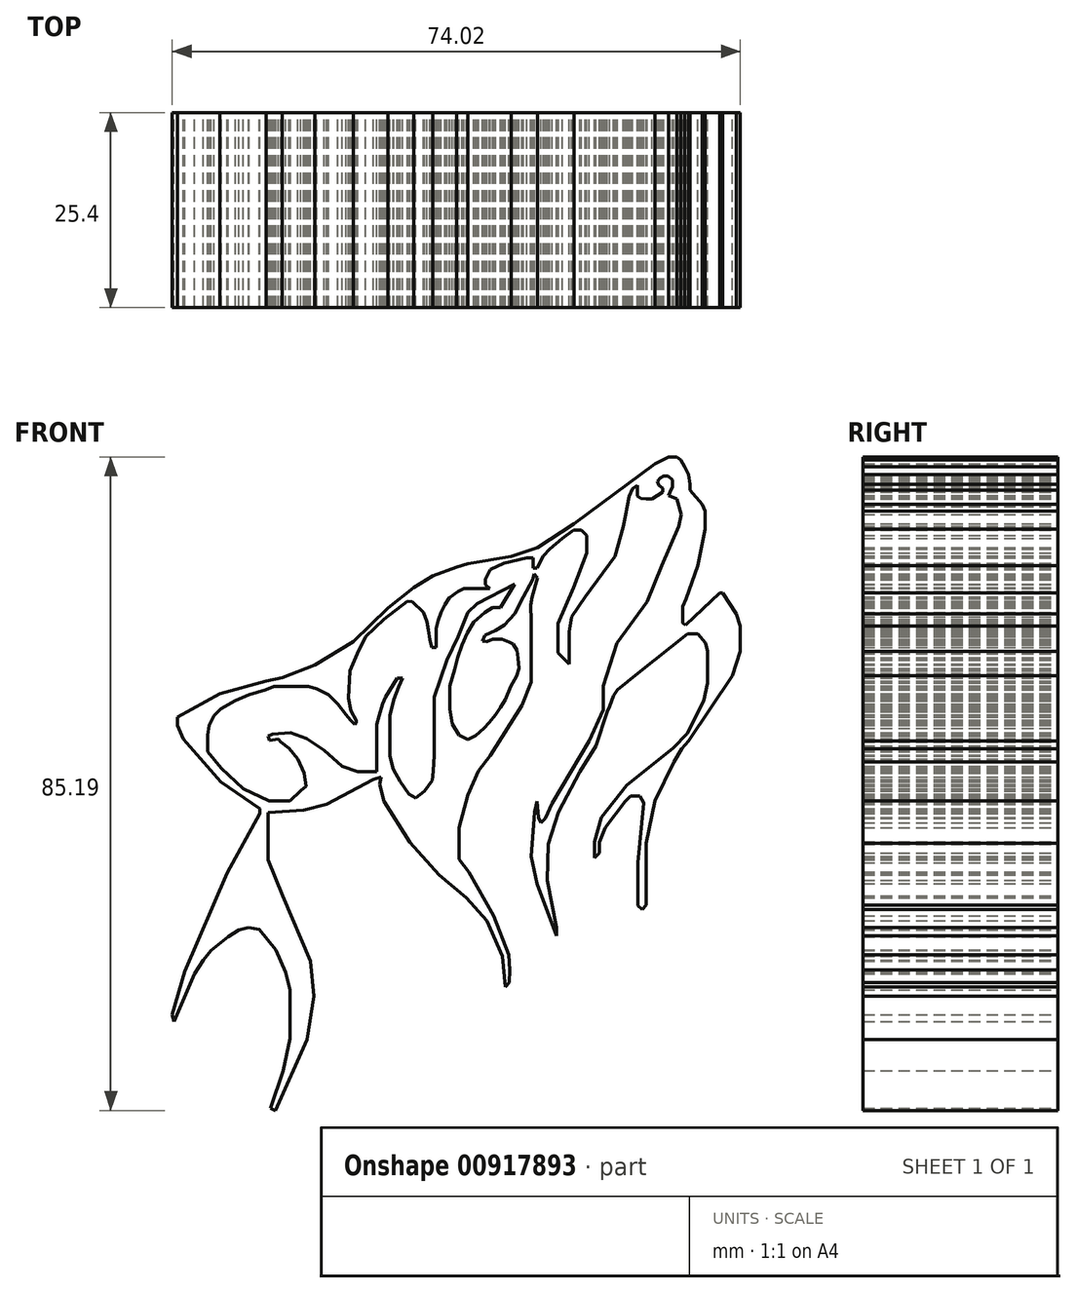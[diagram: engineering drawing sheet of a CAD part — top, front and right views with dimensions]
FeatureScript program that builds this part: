
annotation { "Feature Type Name" : "Feature", "Feature Type Description" : "" }
export const myFeature = defineFeature(function(context is Context, id is Id, definition is map)
    precondition{}
    {
        {
            var Q0;
            Q0=qCreatedBy(makeId("Front.planeOp"),FACE);
            var sketch = newSketch(context, id + "F0", { "sketchPlane" : qUnion([Q0])});
            skLineSegment(sketch, "E0", {"start": v(-38.5, -15.53) * mm, "end": v(-36.88, -9.84) * mm});
            skLineSegment(sketch, "E1", {"start": v(-36.88, -9.84) * mm, "end": v(-31.3, 2.95) * mm});
            skLineSegment(sketch, "E2", {"start": v(-31.3, 2.95) * mm, "end": v(-27.1, 10.73) * mm});
            skLineSegment(sketch, "E3", {"start": v(-27.1, 10.73) * mm, "end": v(-27.1, 11.36) * mm});
            skLineSegment(sketch, "E4", {"start": v(-27.1, 11.36) * mm, "end": v(-32.14, 14.82) * mm});
            skLineSegment(sketch, "E5", {"start": v(-32.14, 14.82) * mm, "end": v(-37.06, 20.41) * mm});
            skLineSegment(sketch, "E6", {"start": v(-37.06, 20.41) * mm, "end": v(-37.8, 22.21) * mm});
            skLineSegment(sketch, "E7", {"start": v(-37.8, 22.21) * mm, "end": v(-37.8, 23.3) * mm});
            skLineSegment(sketch, "E8", {"start": v(-37.8, 23.3) * mm, "end": v(-32.31, 26.36) * mm});
            skLineSegment(sketch, "E9", {"start": v(-32.31, 26.36) * mm, "end": v(-26.28, 28) * mm});
            skLineSegment(sketch, "E10", {"start": v(-26.28, 28) * mm, "end": v(-24.14, 28.41) * mm});
            skLineSegment(sketch, "E11", {"start": v(-24.14, 28.41) * mm, "end": v(-19.93, 30.06) * mm});
            skLineSegment(sketch, "E12", {"start": v(-19.93, 30.06) * mm, "end": v(-14.86, 33.12) * mm});
            skLineSegment(sketch, "E13", {"start": v(-14.86, 33.12) * mm, "end": v(-10.37, 37.53) * mm});
            skLineSegment(sketch, "E14", {"start": v(-10.37, 37.53) * mm, "end": v(-7.02, 40.16) * mm});
            skLineSegment(sketch, "E15", {"start": v(-7.02, 40.16) * mm, "end": v(-4.55, 41.68) * mm});
            skLineSegment(sketch, "E16", {"start": v(-4.55, 41.68) * mm, "end": v(-1.43, 42.86) * mm});
            skLineSegment(sketch, "E17", {"start": v(-1.43, 42.86) * mm, "end": v(0, 43.31) * mm});
            skLineSegment(sketch, "E18", {"start": v(0, 43.31) * mm, "end": v(5.68, 44.23) * mm});
            skLineSegment(sketch, "E19", {"start": v(5.68, 44.23) * mm, "end": v(9.13, 45.4) * mm});
            skLineSegment(sketch, "E20", {"start": v(9.13, 45.4) * mm, "end": v(13.88, 48.46) * mm});
            skLineSegment(sketch, "E21", {"start": v(13.88, 48.46) * mm, "end": v(24.44, 56.3) * mm});
            skLineSegment(sketch, "E22", {"start": v(24.44, 56.3) * mm, "end": v(26.17, 57.2) * mm});
            skLineSegment(sketch, "E23", {"start": v(26.17, 57.2) * mm, "end": v(27.25, 57.2) * mm});
            skLineSegment(sketch, "E24", {"start": v(27.25, 57.2) * mm, "end": v(27.75, 56.8) * mm});
            skLineSegment(sketch, "E25", {"start": v(27.75, 56.8) * mm, "end": v(28.27, 55.93) * mm});
            skLineSegment(sketch, "E26", {"start": v(28.27, 55.93) * mm, "end": v(28.77, 54.9) * mm});
            skLineSegment(sketch, "E27", {"start": v(28.77, 54.9) * mm, "end": v(28.96, 53.66) * mm});
            skLineSegment(sketch, "E28", {"start": v(28.96, 53.66) * mm, "end": v(28.96, 52.88) * mm});
            skLineSegment(sketch, "E29", {"start": v(28.96, 52.88) * mm, "end": v(30.55, 51) * mm});
            skLineSegment(sketch, "E30", {"start": v(30.55, 51) * mm, "end": v(30.97, 50.12) * mm});
            skLineSegment(sketch, "E31", {"start": v(30.97, 50.12) * mm, "end": v(30.97, 47.77) * mm});
            skLineSegment(sketch, "E32", {"start": v(30.97, 47.77) * mm, "end": v(30, 43.06) * mm});
            skLineSegment(sketch, "E33", {"start": v(30, 43.06) * mm, "end": v(28.46, 38.73) * mm});
            skLineSegment(sketch, "E34", {"start": v(28.46, 38.73) * mm, "end": v(28.05, 37.7) * mm});
            skLineSegment(sketch, "E35", {"start": v(28.05, 37.7) * mm, "end": v(28.05, 36.88) * mm});
            skLineSegment(sketch, "E36", {"start": v(28.05, 36.88) * mm, "end": v(28.05, 35.54) * mm});
            skLineSegment(sketch, "E37", {"start": v(28.05, 35.54) * mm, "end": v(28.4, 35.26) * mm});
            skLineSegment(sketch, "E38", {"start": v(28.4, 35.26) * mm, "end": v(32.85, 39.46) * mm});
            skLineSegment(sketch, "E39", {"start": v(32.85, 39.46) * mm, "end": v(33.27, 39.46) * mm});
            skLineSegment(sketch, "E40", {"start": v(33.27, 39.46) * mm, "end": v(35.03, 36.78) * mm});
            skLineSegment(sketch, "E41", {"start": v(35.03, 36.78) * mm, "end": v(35.53, 35.19) * mm});
            skLineSegment(sketch, "E42", {"start": v(35.53, 35.19) * mm, "end": v(35.53, 31.87) * mm});
            skLineSegment(sketch, "E43", {"start": v(35.53, 31.87) * mm, "end": v(34.48, 28.7) * mm});
            skLineSegment(sketch, "E44", {"start": v(34.48, 28.7) * mm, "end": v(32.17, 25.26) * mm});
            skLineSegment(sketch, "E45", {"start": v(32.17, 25.26) * mm, "end": v(28.77, 20.2) * mm});
            skLineSegment(sketch, "E46", {"start": v(28.77, 20.2) * mm, "end": v(27.93, 19.14) * mm});
            skLineSegment(sketch, "E47", {"start": v(27.93, 19.14) * mm, "end": v(26.86, 17.45) * mm});
            skLineSegment(sketch, "E48", {"start": v(26.86, 17.45) * mm, "end": v(24.38, 12.35) * mm});
            skLineSegment(sketch, "E49", {"start": v(24.38, 12.35) * mm, "end": v(23.84, 9.71) * mm});
            skLineSegment(sketch, "E50", {"start": v(23.84, 9.71) * mm, "end": v(23.24, 6.84) * mm});
            skLineSegment(sketch, "E51", {"start": v(23.24, 6.84) * mm, "end": v(23.24, 5.26) * mm});
            skLineSegment(sketch, "E52", {"start": v(23.24, 5.26) * mm, "end": v(23.24, -1.23) * mm});
            skLineSegment(sketch, "E53", {"start": v(23.24, -1.23) * mm, "end": v(22.78, -1.77) * mm});
            skLineSegment(sketch, "E54", {"start": v(22.78, -1.77) * mm, "end": v(22.22, -1.3) * mm});
            skLineSegment(sketch, "E55", {"start": v(22.22, -1.3) * mm, "end": v(22.22, 4.3) * mm});
            skLineSegment(sketch, "E56", {"start": v(22.22, 4.3) * mm, "end": v(22.95, 12.08) * mm});
            skLineSegment(sketch, "E57", {"start": v(22.95, 12.08) * mm, "end": v(22.46, 13) * mm});
            skLineSegment(sketch, "E58", {"start": v(22.46, 13) * mm, "end": v(21.22, 13) * mm});
            skLineSegment(sketch, "E59", {"start": v(21.22, 13) * mm, "end": v(20.51, 12.3) * mm});
            skLineSegment(sketch, "E60", {"start": v(20.51, 12.3) * mm, "end": v(17.91, 8.84) * mm});
            skLineSegment(sketch, "E61", {"start": v(17.91, 8.84) * mm, "end": v(17.16, 6.94) * mm});
            skLineSegment(sketch, "E62", {"start": v(17.16, 6.94) * mm, "end": v(17.16, 5.54) * mm});
            skLineSegment(sketch, "E63", {"start": v(17.16, 5.54) * mm, "end": v(16.56, 4.94) * mm});
            skLineSegment(sketch, "E64", {"start": v(16.56, 4.94) * mm, "end": v(16.56, 7) * mm});
            skLineSegment(sketch, "E65", {"start": v(16.56, 7) * mm, "end": v(17.43, 10.2) * mm});
            skLineSegment(sketch, "E66", {"start": v(17.43, 10.2) * mm, "end": v(20.73, 14.41) * mm});
            skLineSegment(sketch, "E67", {"start": v(20.73, 14.41) * mm, "end": v(26.84, 19.28) * mm});
            skLineSegment(sketch, "E68", {"start": v(26.84, 19.28) * mm, "end": v(28.6, 21.13) * mm});
            skLineSegment(sketch, "E69", {"start": v(28.6, 21.13) * mm, "end": v(30.76, 25.4) * mm});
            skLineSegment(sketch, "E70", {"start": v(30.76, 25.4) * mm, "end": v(31.3, 27.72) * mm});
            skLineSegment(sketch, "E71", {"start": v(31.3, 27.72) * mm, "end": v(31.3, 29.81) * mm});
            skLineSegment(sketch, "E72", {"start": v(31.3, 29.81) * mm, "end": v(31.3, 31.88) * mm});
            skLineSegment(sketch, "E73", {"start": v(31.3, 31.88) * mm, "end": v(31.02, 32.96) * mm});
            skLineSegment(sketch, "E74", {"start": v(31.02, 32.96) * mm, "end": v(29.98, 34.12) * mm});
            skLineSegment(sketch, "E75", {"start": v(29.98, 34.12) * mm, "end": v(28.64, 34.12) * mm});
            skLineSegment(sketch, "E76", {"start": v(28.64, 34.12) * mm, "end": v(22.17, 29.01) * mm});
            skLineSegment(sketch, "E77", {"start": v(22.17, 29.01) * mm, "end": v(19.53, 26.84) * mm});
            skLineSegment(sketch, "E78", {"start": v(19.53, 26.84) * mm, "end": v(19.02, 26.1) * mm});
            skLineSegment(sketch, "E79", {"start": v(19.02, 26.1) * mm, "end": v(18.48, 24.67) * mm});
            skLineSegment(sketch, "E80", {"start": v(18.48, 24.67) * mm, "end": v(18.18, 24) * mm});
            skLineSegment(sketch, "E81", {"start": v(18.18, 24) * mm, "end": v(17.67, 24.23) * mm});
            skLineSegment(sketch, "E82", {"start": v(17.67, 24.23) * mm, "end": v(17.67, 27.37) * mm});
            skLineSegment(sketch, "E83", {"start": v(17.67, 27.37) * mm, "end": v(19.45, 32.92) * mm});
            skLineSegment(sketch, "E84", {"start": v(19.45, 32.92) * mm, "end": v(23.42, 38.36) * mm});
            skLineSegment(sketch, "E85", {"start": v(23.42, 38.36) * mm, "end": v(25.3, 43.03) * mm});
            skLineSegment(sketch, "E86", {"start": v(25.3, 43.03) * mm, "end": v(27.5, 48.16) * mm});
            skLineSegment(sketch, "E87", {"start": v(27.5, 48.16) * mm, "end": v(27.86, 49.72) * mm});
            skLineSegment(sketch, "E88", {"start": v(27.86, 49.72) * mm, "end": v(27.25, 51.74) * mm});
            skLineSegment(sketch, "E89", {"start": v(27.25, 51.74) * mm, "end": v(26.17, 52.2) * mm});
            skLineSegment(sketch, "E90", {"start": v(26.17, 52.2) * mm, "end": v(26.35, 52.6) * mm});
            skLineSegment(sketch, "E91", {"start": v(26.35, 52.6) * mm, "end": v(26.7, 53.3) * mm});
            skLineSegment(sketch, "E92", {"start": v(26.7, 53.3) * mm, "end": v(26.7, 54.22) * mm});
            skLineSegment(sketch, "E93", {"start": v(26.7, 54.22) * mm, "end": v(26.15, 54.7) * mm});
            skLineSegment(sketch, "E94", {"start": v(26.15, 54.7) * mm, "end": v(25.56, 54.7) * mm});
            skLineSegment(sketch, "E95", {"start": v(25.56, 54.7) * mm, "end": v(25.08, 54.48) * mm});
            skLineSegment(sketch, "E96", {"start": v(25.08, 54.48) * mm, "end": v(24.72, 54.04) * mm});
            skLineSegment(sketch, "E97", {"start": v(24.72, 54.04) * mm, "end": v(24.94, 53.52) * mm});
            skLineSegment(sketch, "E98", {"start": v(24.94, 53.52) * mm, "end": v(25.42, 53.15) * mm});
            skLineSegment(sketch, "E99", {"start": v(25.42, 53.15) * mm, "end": v(25.42, 52.6) * mm});
            skLineSegment(sketch, "E100", {"start": v(25.42, 52.6) * mm, "end": v(24.01, 51.72) * mm});
            skLineSegment(sketch, "E101", {"start": v(24.01, 51.72) * mm, "end": v(23.28, 51.72) * mm});
            skLineSegment(sketch, "E102", {"start": v(23.28, 51.72) * mm, "end": v(22.54, 51.79) * mm});
            skLineSegment(sketch, "E103", {"start": v(22.54, 51.79) * mm, "end": v(22.13, 52.12) * mm});
            skLineSegment(sketch, "E104", {"start": v(22.13, 52.12) * mm, "end": v(22.1, 52.86) * mm});
            skLineSegment(sketch, "E105", {"start": v(22.1, 52.86) * mm, "end": v(22.1, 53.52) * mm});
            skLineSegment(sketch, "E106", {"start": v(22.1, 53.52) * mm, "end": v(21.47, 53.04) * mm});
            skLineSegment(sketch, "E107", {"start": v(21.47, 53.04) * mm, "end": v(21.03, 52.05) * mm});
            skLineSegment(sketch, "E108", {"start": v(21.03, 52.05) * mm, "end": v(20.8, 50.72) * mm});
            skLineSegment(sketch, "E109", {"start": v(20.8, 50.72) * mm, "end": v(20.62, 49.72) * mm});
            skLineSegment(sketch, "E110", {"start": v(20.62, 49.72) * mm, "end": v(20.29, 48.1) * mm});
            skLineSegment(sketch, "E111", {"start": v(20.29, 48.1) * mm, "end": v(19.22, 44.27) * mm});
            skLineSegment(sketch, "E112", {"start": v(19.22, 44.27) * mm, "end": v(15.35, 38.95) * mm});
            skLineSegment(sketch, "E113", {"start": v(15.35, 38.95) * mm, "end": v(13.54, 36.37) * mm});
            skLineSegment(sketch, "E114", {"start": v(13.54, 36.37) * mm, "end": v(13.2, 34.38) * mm});
            skLineSegment(sketch, "E115", {"start": v(13.2, 34.38) * mm, "end": v(13.2, 31.28) * mm});
            skLineSegment(sketch, "E116", {"start": v(13.2, 31.28) * mm, "end": v(13.2, 30.2) * mm});
            skLineSegment(sketch, "E117", {"start": v(13.2, 30.2) * mm, "end": v(11.8, 31.65) * mm});
            skLineSegment(sketch, "E118", {"start": v(11.8, 31.65) * mm, "end": v(11.8, 35.45) * mm});
            skLineSegment(sketch, "E119", {"start": v(11.8, 35.45) * mm, "end": v(13.79, 40.15) * mm});
            skLineSegment(sketch, "E120", {"start": v(13.79, 40.15) * mm, "end": v(15.55, 44.66) * mm});
            skLineSegment(sketch, "E121", {"start": v(15.55, 44.66) * mm, "end": v(15.55, 46.96) * mm});
            skLineSegment(sketch, "E122", {"start": v(15.55, 46.96) * mm, "end": v(14.81, 47.7) * mm});
            skLineSegment(sketch, "E123", {"start": v(14.81, 47.7) * mm, "end": v(13.78, 47.7) * mm});
            skLineSegment(sketch, "E124", {"start": v(13.78, 47.7) * mm, "end": v(12.37, 46.56) * mm});
            skLineSegment(sketch, "E125", {"start": v(12.37, 46.56) * mm, "end": v(10.73, 45.2) * mm});
            skLineSegment(sketch, "E126", {"start": v(10.73, 45.2) * mm, "end": v(9.88, 44.3) * mm});
            skLineSegment(sketch, "E127", {"start": v(9.88, 44.3) * mm, "end": v(9.03, 42.71) * mm});
            skLineSegment(sketch, "E128", {"start": v(9.03, 42.71) * mm, "end": v(8.56, 42.71) * mm});
            skLineSegment(sketch, "E129", {"start": v(8.56, 42.71) * mm, "end": v(8.56, 44.03) * mm});
            skLineSegment(sketch, "E130", {"start": v(8.56, 44.03) * mm, "end": v(7.72, 44.03) * mm});
            skLineSegment(sketch, "E131", {"start": v(7.72, 44.03) * mm, "end": v(4.71, 43.37) * mm});
            skLineSegment(sketch, "E132", {"start": v(4.71, 43.37) * mm, "end": v(2.98, 42.53) * mm});
            skLineSegment(sketch, "E133", {"start": v(2.98, 42.53) * mm, "end": v(2.32, 41.26) * mm});
            skLineSegment(sketch, "E134", {"start": v(2.32, 41.26) * mm, "end": v(2.32, 40.55) * mm});
            skLineSegment(sketch, "E135", {"start": v(2.32, 40.55) * mm, "end": v(2.88, 40.04) * mm});
            skLineSegment(sketch, "E136", {"start": v(2.88, 40.04) * mm, "end": v(-0.45, 40.04) * mm});
            skLineSegment(sketch, "E137", {"start": v(-0.45, 40.04) * mm, "end": v(-1.26, 39.64) * mm});
            skLineSegment(sketch, "E138", {"start": v(-1.26, 39.64) * mm, "end": v(-2.36, 38.86) * mm});
            skLineSegment(sketch, "E139", {"start": v(-2.36, 38.86) * mm, "end": v(-2.95, 37.97) * mm});
            skLineSegment(sketch, "E140", {"start": v(-2.95, 37.97) * mm, "end": v(-3.5, 36.97) * mm});
            skLineSegment(sketch, "E141", {"start": v(-3.5, 36.97) * mm, "end": v(-3.86, 35.84) * mm});
            skLineSegment(sketch, "E142", {"start": v(-3.86, 35.84) * mm, "end": v(-4.08, 34.86) * mm});
            skLineSegment(sketch, "E143", {"start": v(-4.08, 34.86) * mm, "end": v(-4.08, 33.83) * mm});
            skLineSegment(sketch, "E144", {"start": v(-4.08, 33.83) * mm, "end": v(-4.08, 32.35) * mm});
            skLineSegment(sketch, "E145", {"start": v(-4.08, 32.35) * mm, "end": v(-4.65, 32.35) * mm});
            skLineSegment(sketch, "E146", {"start": v(-4.65, 32.35) * mm, "end": v(-4.92, 33.36) * mm});
            skLineSegment(sketch, "E147", {"start": v(-4.92, 33.36) * mm, "end": v(-5.14, 34.64) * mm});
            skLineSegment(sketch, "E148", {"start": v(-5.14, 34.64) * mm, "end": v(-5.33, 35.72) * mm});
            skLineSegment(sketch, "E149", {"start": v(-5.33, 35.72) * mm, "end": v(-5.73, 36.97) * mm});
            skLineSegment(sketch, "E150", {"start": v(-5.73, 36.97) * mm, "end": v(-7.2, 38.34) * mm});
            skLineSegment(sketch, "E151", {"start": v(-7.2, 38.34) * mm, "end": v(-7.86, 38.37) * mm});
            skLineSegment(sketch, "E152", {"start": v(-7.86, 38.37) * mm, "end": v(-10.93, 36.06) * mm});
            skLineSegment(sketch, "E153", {"start": v(-10.93, 36.06) * mm, "end": v(-13.28, 33.75) * mm});
            skLineSegment(sketch, "E154", {"start": v(-13.28, 33.75) * mm, "end": v(-14.4, 31.5) * mm});
            skLineSegment(sketch, "E155", {"start": v(-14.4, 31.5) * mm, "end": v(-15.3, 29.3) * mm});
            skLineSegment(sketch, "E156", {"start": v(-15.3, 29.3) * mm, "end": v(-15.54, 25.76) * mm});
            skLineSegment(sketch, "E157", {"start": v(-15.54, 25.76) * mm, "end": v(-15.24, 24.1) * mm});
            skLineSegment(sketch, "E158", {"start": v(-15.24, 24.1) * mm, "end": v(-14.54, 22.83) * mm});
            skLineSegment(sketch, "E159", {"start": v(-14.54, 22.83) * mm, "end": v(-14.54, 22.53) * mm});
            skLineSegment(sketch, "E160", {"start": v(-14.54, 22.53) * mm, "end": v(-14.72, 22.34) * mm});
            skLineSegment(sketch, "E161", {"start": v(-14.72, 22.34) * mm, "end": v(-15.27, 22.9) * mm});
            skLineSegment(sketch, "E162", {"start": v(-15.27, 22.9) * mm, "end": v(-15.87, 23.63) * mm});
            skLineSegment(sketch, "E163", {"start": v(-15.87, 23.63) * mm, "end": v(-16.93, 24.97) * mm});
            skLineSegment(sketch, "E164", {"start": v(-16.93, 24.97) * mm, "end": v(-18.1, 26.2) * mm});
            skLineSegment(sketch, "E165", {"start": v(-18.1, 26.2) * mm, "end": v(-19.67, 26.98) * mm});
            skLineSegment(sketch, "E166", {"start": v(-19.67, 26.98) * mm, "end": v(-20.73, 27.29) * mm});
            skLineSegment(sketch, "E167", {"start": v(-20.73, 27.29) * mm, "end": v(-25.27, 27.29) * mm});
            skLineSegment(sketch, "E168", {"start": v(-25.27, 27.29) * mm, "end": v(-26.35, 26.84) * mm});
            skLineSegment(sketch, "E169", {"start": v(-26.35, 26.84) * mm, "end": v(-28.49, 26.19) * mm});
            skLineSegment(sketch, "E170", {"start": v(-28.49, 26.19) * mm, "end": v(-30.24, 25.44) * mm});
            skLineSegment(sketch, "E171", {"start": v(-30.24, 25.44) * mm, "end": v(-32.14, 24.4) * mm});
            skLineSegment(sketch, "E172", {"start": v(-32.14, 24.4) * mm, "end": v(-33.05, 23.5) * mm});
            skLineSegment(sketch, "E173", {"start": v(-33.05, 23.5) * mm, "end": v(-33.66, 22.2) * mm});
            skLineSegment(sketch, "E174", {"start": v(-33.66, 22.2) * mm, "end": v(-33.87, 20.9) * mm});
            skLineSegment(sketch, "E175", {"start": v(-33.87, 20.9) * mm, "end": v(-33.87, 18.78) * mm});
            skLineSegment(sketch, "E176", {"start": v(-33.87, 18.78) * mm, "end": v(-32.1, 16.6) * mm});
            skLineSegment(sketch, "E177", {"start": v(-32.1, 16.6) * mm, "end": v(-29.22, 13.93) * mm});
            skLineSegment(sketch, "E178", {"start": v(-29.22, 13.93) * mm, "end": v(-25.87, 12.36) * mm});
            skLineSegment(sketch, "E179", {"start": v(-25.87, 12.36) * mm, "end": v(-23.13, 12.36) * mm});
            skLineSegment(sketch, "E180", {"start": v(-23.13, 12.36) * mm, "end": v(-21.76, 13.72) * mm});
            skLineSegment(sketch, "E181", {"start": v(-21.76, 13.72) * mm, "end": v(-21.08, 14.27) * mm});
            skLineSegment(sketch, "E182", {"start": v(-21.08, 14.27) * mm, "end": v(-21.29, 15.98) * mm});
            skLineSegment(sketch, "E183", {"start": v(-21.29, 15.98) * mm, "end": v(-22.1, 17.83) * mm});
            skLineSegment(sketch, "E184", {"start": v(-22.1, 17.83) * mm, "end": v(-23.27, 19.2) * mm});
            skLineSegment(sketch, "E185", {"start": v(-23.27, 19.2) * mm, "end": v(-24.36, 20.02) * mm});
            skLineSegment(sketch, "E186", {"start": v(-24.36, 20.02) * mm, "end": v(-24.7, 20.43) * mm});
            skLineSegment(sketch, "E187", {"start": v(-24.7, 20.43) * mm, "end": v(-25.8, 20.22) * mm});
            skLineSegment(sketch, "E188", {"start": v(-25.8, 20.22) * mm, "end": v(-26, 20.84) * mm});
            skLineSegment(sketch, "E189", {"start": v(-26, 20.84) * mm, "end": v(-25.4, 21.03) * mm});
            skLineSegment(sketch, "E190", {"start": v(-25.4, 21.03) * mm, "end": v(-23.06, 21.25) * mm});
            skLineSegment(sketch, "E191", {"start": v(-23.06, 21.25) * mm, "end": v(-21.01, 20.5) * mm});
            skLineSegment(sketch, "E192", {"start": v(-21.01, 20.5) * mm, "end": v(-18.69, 18.99) * mm});
            skLineSegment(sketch, "E193", {"start": v(-18.69, 18.99) * mm, "end": v(-16.36, 16.87) * mm});
            skLineSegment(sketch, "E194", {"start": v(-16.36, 16.87) * mm, "end": v(-14.3, 16.19) * mm});
            skLineSegment(sketch, "E195", {"start": v(-14.3, 16.19) * mm, "end": v(-12.67, 16.19) * mm});
            skLineSegment(sketch, "E196", {"start": v(-12.67, 16.19) * mm, "end": v(-11.85, 16.19) * mm});
            skLineSegment(sketch, "E197", {"start": v(-11.85, 16.19) * mm, "end": v(-11.85, 18.86) * mm});
            skLineSegment(sketch, "E198", {"start": v(-11.85, 18.86) * mm, "end": v(-11.83, 20.73) * mm});
            skLineSegment(sketch, "E199", {"start": v(-11.83, 20.73) * mm, "end": v(-11.83, 22.32) * mm});
            skLineSegment(sketch, "E200", {"start": v(-11.83, 22.32) * mm, "end": v(-11.51, 23.5) * mm});
            skLineSegment(sketch, "E201", {"start": v(-11.51, 23.5) * mm, "end": v(-11.1, 25) * mm});
            skLineSegment(sketch, "E202", {"start": v(-11.1, 25) * mm, "end": v(-10.67, 25.9) * mm});
            skLineSegment(sketch, "E203", {"start": v(-10.67, 25.9) * mm, "end": v(-9.16, 28.35) * mm});
            skLineSegment(sketch, "E204", {"start": v(-9.16, 28.35) * mm, "end": v(-8.5, 28.35) * mm});
            skLineSegment(sketch, "E205", {"start": v(-8.5, 28.35) * mm, "end": v(-9, 27.23) * mm});
            skLineSegment(sketch, "E206", {"start": v(-9, 27.23) * mm, "end": v(-9.6, 25.55) * mm});
            skLineSegment(sketch, "E207", {"start": v(-9.6, 25.55) * mm, "end": v(-10.12, 23.47) * mm});
            skLineSegment(sketch, "E208", {"start": v(-10.12, 23.47) * mm, "end": v(-10.12, 19.92) * mm});
            skLineSegment(sketch, "E209", {"start": v(-10.12, 19.92) * mm, "end": v(-10.12, 18.2) * mm});
            skLineSegment(sketch, "E210", {"start": v(-10.12, 18.2) * mm, "end": v(-9.66, 16.47) * mm});
            skLineSegment(sketch, "E211", {"start": v(-9.66, 16.47) * mm, "end": v(-8.8, 14.9) * mm});
            skLineSegment(sketch, "E212", {"start": v(-8.8, 14.9) * mm, "end": v(-7.68, 13.27) * mm});
            skLineSegment(sketch, "E213", {"start": v(-7.68, 13.27) * mm, "end": v(-6.77, 12.72) * mm});
            skLineSegment(sketch, "E214", {"start": v(-6.77, 12.72) * mm, "end": v(-5.65, 13.63) * mm});
            skLineSegment(sketch, "E215", {"start": v(-5.65, 13.63) * mm, "end": v(-4.59, 15.05) * mm});
            skLineSegment(sketch, "E216", {"start": v(-4.59, 15.05) * mm, "end": v(-4.48, 16.22) * mm});
            skLineSegment(sketch, "E217", {"start": v(-4.48, 16.22) * mm, "end": v(-4.33, 18.35) * mm});
            skLineSegment(sketch, "E218", {"start": v(-4.33, 18.35) * mm, "end": v(-4.33, 23.37) * mm});
            skLineSegment(sketch, "E219", {"start": v(-4.33, 23.37) * mm, "end": v(-4.33, 25.9) * mm});
            skLineSegment(sketch, "E220", {"start": v(-4.33, 25.9) * mm, "end": v(-2.7, 30.73) * mm});
            skLineSegment(sketch, "E221", {"start": v(-2.7, 30.73) * mm, "end": v(-1.26, 33.75) * mm});
            skLineSegment(sketch, "E222", {"start": v(-1.26, 33.75) * mm, "end": v(0, 36.92) * mm});
            skLineSegment(sketch, "E223", {"start": v(0, 36.92) * mm, "end": v(1.24, 38.1) * mm});
            skLineSegment(sketch, "E224", {"start": v(1.24, 38.1) * mm, "end": v(6.12, 40.6) * mm});
            skLineSegment(sketch, "E225", {"start": v(6.12, 40.6) * mm, "end": v(4.28, 37.57) * mm});
            skLineSegment(sketch, "E226", {"start": v(4.28, 37.57) * mm, "end": v(3.24, 37.57) * mm});
            skLineSegment(sketch, "E227", {"start": v(3.24, 37.57) * mm, "end": v(2.27, 36.96) * mm});
            skLineSegment(sketch, "E228", {"start": v(2.27, 36.96) * mm, "end": v(0.76, 35.7) * mm});
            skLineSegment(sketch, "E229", {"start": v(0.76, 35.7) * mm, "end": v(-0.06, 34.29) * mm});
            skLineSegment(sketch, "E230", {"start": v(-0.06, 34.29) * mm, "end": v(-0.74, 32.69) * mm});
            skLineSegment(sketch, "E231", {"start": v(-0.74, 32.69) * mm, "end": v(-1.32, 31.04) * mm});
            skLineSegment(sketch, "E232", {"start": v(-1.32, 31.04) * mm, "end": v(-1.71, 29.48) * mm});
            skLineSegment(sketch, "E233", {"start": v(-1.71, 29.48) * mm, "end": v(-2.3, 27.35) * mm});
            skLineSegment(sketch, "E234", {"start": v(-2.3, 27.35) * mm, "end": v(-2.3, 24.39) * mm});
            skLineSegment(sketch, "E235", {"start": v(-2.3, 24.39) * mm, "end": v(-2, 22.4) * mm});
            skLineSegment(sketch, "E236", {"start": v(-2, 22.4) * mm, "end": v(-1.13, 20.94) * mm});
            skLineSegment(sketch, "E237", {"start": v(-1.13, 20.94) * mm, "end": v(0, 20.36) * mm});
            skLineSegment(sketch, "E238", {"start": v(0, 20.36) * mm, "end": v(1.05, 20.9) * mm});
            skLineSegment(sketch, "E239", {"start": v(1.05, 20.9) * mm, "end": v(2.12, 21.82) * mm});
            skLineSegment(sketch, "E240", {"start": v(2.12, 21.82) * mm, "end": v(2.8, 22.6) * mm});
            skLineSegment(sketch, "E241", {"start": v(2.8, 22.6) * mm, "end": v(3.63, 23.61) * mm});
            skLineSegment(sketch, "E242", {"start": v(3.63, 23.61) * mm, "end": v(4.26, 24.54) * mm});
            skLineSegment(sketch, "E243", {"start": v(4.26, 24.54) * mm, "end": v(4.94, 25.55) * mm});
            skLineSegment(sketch, "E244", {"start": v(4.94, 25.55) * mm, "end": v(5.62, 27.25) * mm});
            skLineSegment(sketch, "E245", {"start": v(5.62, 27.25) * mm, "end": v(6.4, 28.61) * mm});
            skLineSegment(sketch, "E246", {"start": v(6.4, 28.61) * mm, "end": v(6.68, 29.63) * mm});
            skLineSegment(sketch, "E247", {"start": v(6.68, 29.63) * mm, "end": v(6.59, 30.94) * mm});
            skLineSegment(sketch, "E248", {"start": v(6.59, 30.94) * mm, "end": v(6.44, 31.96) * mm});
            skLineSegment(sketch, "E249", {"start": v(6.44, 31.96) * mm, "end": v(5.9, 32.78) * mm});
            skLineSegment(sketch, "E250", {"start": v(5.9, 32.78) * mm, "end": v(5.42, 33.08) * mm});
            skLineSegment(sketch, "E251", {"start": v(5.42, 33.08) * mm, "end": v(4.5, 33.42) * mm});
            skLineSegment(sketch, "E252", {"start": v(4.5, 33.42) * mm, "end": v(3.24, 33.42) * mm});
            skLineSegment(sketch, "E253", {"start": v(3.24, 33.42) * mm, "end": v(2.5, 33.12) * mm});
            skLineSegment(sketch, "E254", {"start": v(2.5, 33.12) * mm, "end": v(1.93, 33.22) * mm});
            skLineSegment(sketch, "E255", {"start": v(1.93, 33.22) * mm, "end": v(2.27, 33.95) * mm});
            skLineSegment(sketch, "E256", {"start": v(2.27, 33.95) * mm, "end": v(3.63, 34.58) * mm});
            skLineSegment(sketch, "E257", {"start": v(3.63, 34.58) * mm, "end": v(4.8, 35.3) * mm});
            skLineSegment(sketch, "E258", {"start": v(4.8, 35.3) * mm, "end": v(6.15, 36.76) * mm});
            skLineSegment(sketch, "E259", {"start": v(6.15, 36.76) * mm, "end": v(7.27, 38.95) * mm});
            skLineSegment(sketch, "E260", {"start": v(7.27, 38.95) * mm, "end": v(8.48, 41.18) * mm});
            skLineSegment(sketch, "E261", {"start": v(8.48, 41.18) * mm, "end": v(8.67, 41.96) * mm});
            skLineSegment(sketch, "E262", {"start": v(8.67, 41.96) * mm, "end": v(9.1, 41.42) * mm});
            skLineSegment(sketch, "E263", {"start": v(9.1, 41.42) * mm, "end": v(8.43, 39) * mm});
            skLineSegment(sketch, "E264", {"start": v(8.43, 39) * mm, "end": v(8.19, 37.88) * mm});
            skLineSegment(sketch, "E265", {"start": v(8.19, 37.88) * mm, "end": v(8.28, 35.8) * mm});
            skLineSegment(sketch, "E266", {"start": v(8.28, 35.8) * mm, "end": v(8.28, 27.88) * mm});
            skLineSegment(sketch, "E267", {"start": v(8.28, 27.88) * mm, "end": v(7.07, 24.83) * mm});
            skLineSegment(sketch, "E268", {"start": v(7.07, 24.83) * mm, "end": v(2.95, 18.28) * mm});
            skLineSegment(sketch, "E269", {"start": v(2.95, 18.28) * mm, "end": v(1.44, 16.29) * mm});
            skLineSegment(sketch, "E270", {"start": v(1.44, 16.29) * mm, "end": v(0, 13.1) * mm});
            skLineSegment(sketch, "E271", {"start": v(0, 13.1) * mm, "end": v(-1.11, 8.88) * mm});
            skLineSegment(sketch, "E272", {"start": v(-1.11, 8.88) * mm, "end": v(-1.11, 4.77) * mm});
            skLineSegment(sketch, "E273", {"start": v(-1.11, 4.77) * mm, "end": v(0.17, 3.1) * mm});
            skLineSegment(sketch, "E274", {"start": v(0.17, 3.1) * mm, "end": v(3.37, -2.63) * mm});
            skLineSegment(sketch, "E275", {"start": v(3.37, -2.63) * mm, "end": v(5.36, -7.73) * mm});
            skLineSegment(sketch, "E276", {"start": v(5.36, -7.73) * mm, "end": v(5.48, -9.66) * mm});
            skLineSegment(sketch, "E277", {"start": v(5.48, -9.66) * mm, "end": v(5.42, -11.33) * mm});
            skLineSegment(sketch, "E278", {"start": v(5.42, -11.33) * mm, "end": v(4.92, -11.89) * mm});
            skLineSegment(sketch, "E279", {"start": v(4.92, -11.89) * mm, "end": v(4.55, -7.92) * mm});
            skLineSegment(sketch, "E280", {"start": v(4.55, -7.92) * mm, "end": v(2.5, -3.26) * mm});
            skLineSegment(sketch, "E281", {"start": v(2.5, -3.26) * mm, "end": v(-0.16, -0.29) * mm});
            skLineSegment(sketch, "E282", {"start": v(-0.16, -0.29) * mm, "end": v(-3.7, 2.7) * mm});
            skLineSegment(sketch, "E283", {"start": v(-3.7, 2.7) * mm, "end": v(-7.55, 6.98) * mm});
            skLineSegment(sketch, "E284", {"start": v(-7.55, 6.98) * mm, "end": v(-10.9, 12.31) * mm});
            skLineSegment(sketch, "E285", {"start": v(-10.9, 12.31) * mm, "end": v(-11.46, 14.55) * mm});
            skLineSegment(sketch, "E286", {"start": v(-11.46, 14.55) * mm, "end": v(-11.27, 15.48) * mm});
            skLineSegment(sketch, "E287", {"start": v(-11.27, 15.48) * mm, "end": v(-12.27, 15.17) * mm});
            skLineSegment(sketch, "E288", {"start": v(-12.27, 15.17) * mm, "end": v(-18.4, 11.94) * mm});
            skLineSegment(sketch, "E289", {"start": v(-18.4, 11.94) * mm, "end": v(-21.39, 11.13) * mm});
            skLineSegment(sketch, "E290", {"start": v(-21.39, 11.13) * mm, "end": v(-26, 10.84) * mm});
            skLineSegment(sketch, "E291", {"start": v(-26, 10.84) * mm, "end": v(-26, 9.5) * mm});
            skLineSegment(sketch, "E292", {"start": v(-26, 9.5) * mm, "end": v(-26, 7.8) * mm});
            skLineSegment(sketch, "E293", {"start": v(-26, 7.8) * mm, "end": v(-26, 4.68) * mm});
            skLineSegment(sketch, "E294", {"start": v(-26, 4.68) * mm, "end": v(-24.08, 0) * mm});
            skLineSegment(sketch, "E295", {"start": v(-24.08, 0) * mm, "end": v(-20.46, -8.54) * mm});
            skLineSegment(sketch, "E296", {"start": v(-20.46, -8.54) * mm, "end": v(-20.02, -13.13) * mm});
            skLineSegment(sketch, "E297", {"start": v(-20.02, -13.13) * mm, "end": v(-20.95, -18.78) * mm});
            skLineSegment(sketch, "E298", {"start": v(-20.95, -18.78) * mm, "end": v(-25.07, -28) * mm});
            skLineSegment(sketch, "E299", {"start": v(-25.07, -28) * mm, "end": v(-25.67, -27.73) * mm});
            skLineSegment(sketch, "E300", {"start": v(-25.67, -27.73) * mm, "end": v(-24.04, -22.84) * mm});
            skLineSegment(sketch, "E301", {"start": v(-24.04, -22.84) * mm, "end": v(-23.18, -18.65) * mm});
            skLineSegment(sketch, "E302", {"start": v(-23.18, -18.65) * mm, "end": v(-23.18, -12.26) * mm});
            skLineSegment(sketch, "E303", {"start": v(-23.18, -12.26) * mm, "end": v(-23.74, -10.02) * mm});
            skLineSegment(sketch, "E304", {"start": v(-23.74, -10.02) * mm, "end": v(-25.02, -7.08) * mm});
            skLineSegment(sketch, "E305", {"start": v(-25.02, -7.08) * mm, "end": v(-27.12, -4.4) * mm});
            skLineSegment(sketch, "E306", {"start": v(-27.12, -4.4) * mm, "end": v(-28.55, -4.17) * mm});
            skLineSegment(sketch, "E307", {"start": v(-28.55, -4.17) * mm, "end": v(-29.84, -4.45) * mm});
            skLineSegment(sketch, "E308", {"start": v(-29.84, -4.45) * mm, "end": v(-31.22, -5.36) * mm});
            skLineSegment(sketch, "E309", {"start": v(-31.22, -5.36) * mm, "end": v(-33.42, -7.13) * mm});
            skLineSegment(sketch, "E310", {"start": v(-33.42, -7.13) * mm, "end": v(-34.47, -8.41) * mm});
            skLineSegment(sketch, "E311", {"start": v(-34.47, -8.41) * mm, "end": v(-35.61, -10.18) * mm});
            skLineSegment(sketch, "E312", {"start": v(-35.61, -10.18) * mm, "end": v(-38.23, -16.38) * mm});
            skLineSegment(sketch, "E313", {"start": v(-38.23, -16.38) * mm, "end": v(-38.5, -15.53) * mm});
            skLineSegment(sketch, "E314", {"start": v(17.67, 24.23) * mm, "end": v(15.83, 20.15) * mm});
            skLineSegment(sketch, "E315", {"start": v(15.83, 20.15) * mm, "end": v(11.04, 12.07) * mm});
            skLineSegment(sketch, "E316", {"start": v(11.04, 12.07) * mm, "end": v(10.1, 10.06) * mm});
            skLineSegment(sketch, "E317", {"start": v(10.1, 10.06) * mm, "end": v(9.54, 9.53) * mm});
            skLineSegment(sketch, "E318", {"start": v(9.54, 9.53) * mm, "end": v(9.23, 10.2) * mm});
            skLineSegment(sketch, "E319", {"start": v(9.23, 10.2) * mm, "end": v(9.05, 12.32) * mm});
            skLineSegment(sketch, "E320", {"start": v(9.05, 12.32) * mm, "end": v(8.74, 10.88) * mm});
            skLineSegment(sketch, "E321", {"start": v(8.74, 10.88) * mm, "end": v(8.28, 5.1) * mm});
            skLineSegment(sketch, "E322", {"start": v(8.28, 5.1) * mm, "end": v(9.05, 1.58) * mm});
            skLineSegment(sketch, "E323", {"start": v(9.05, 1.58) * mm, "end": v(11.58, -5.26) * mm});
            skLineSegment(sketch, "E324", {"start": v(11.58, -5.26) * mm, "end": v(11.58, -4.12) * mm});
            skLineSegment(sketch, "E325", {"start": v(11.58, -4.12) * mm, "end": v(10.35, 2) * mm});
            skLineSegment(sketch, "E326", {"start": v(10.35, 2) * mm, "end": v(10.53, 6.72) * mm});
            skLineSegment(sketch, "E327", {"start": v(10.53, 6.72) * mm, "end": v(11.84, 10.9) * mm});
            skLineSegment(sketch, "E328", {"start": v(11.84, 10.9) * mm, "end": v(14.64, 16.15) * mm});
            skLineSegment(sketch, "E329", {"start": v(14.64, 16.15) * mm, "end": v(16.73, 19.56) * mm});
            skLineSegment(sketch, "E330", {"start": v(16.73, 19.56) * mm, "end": v(18.18, 24) * mm});
            skSolve(sketch);
        }
        {
            var Q0;
            Q0=qSketchRegion(id+"F0",true);
            extrude(context, id + "F1", {"entities" : qUnion([Q0]), "depth" : 25.4 * mm});
        }
    });
